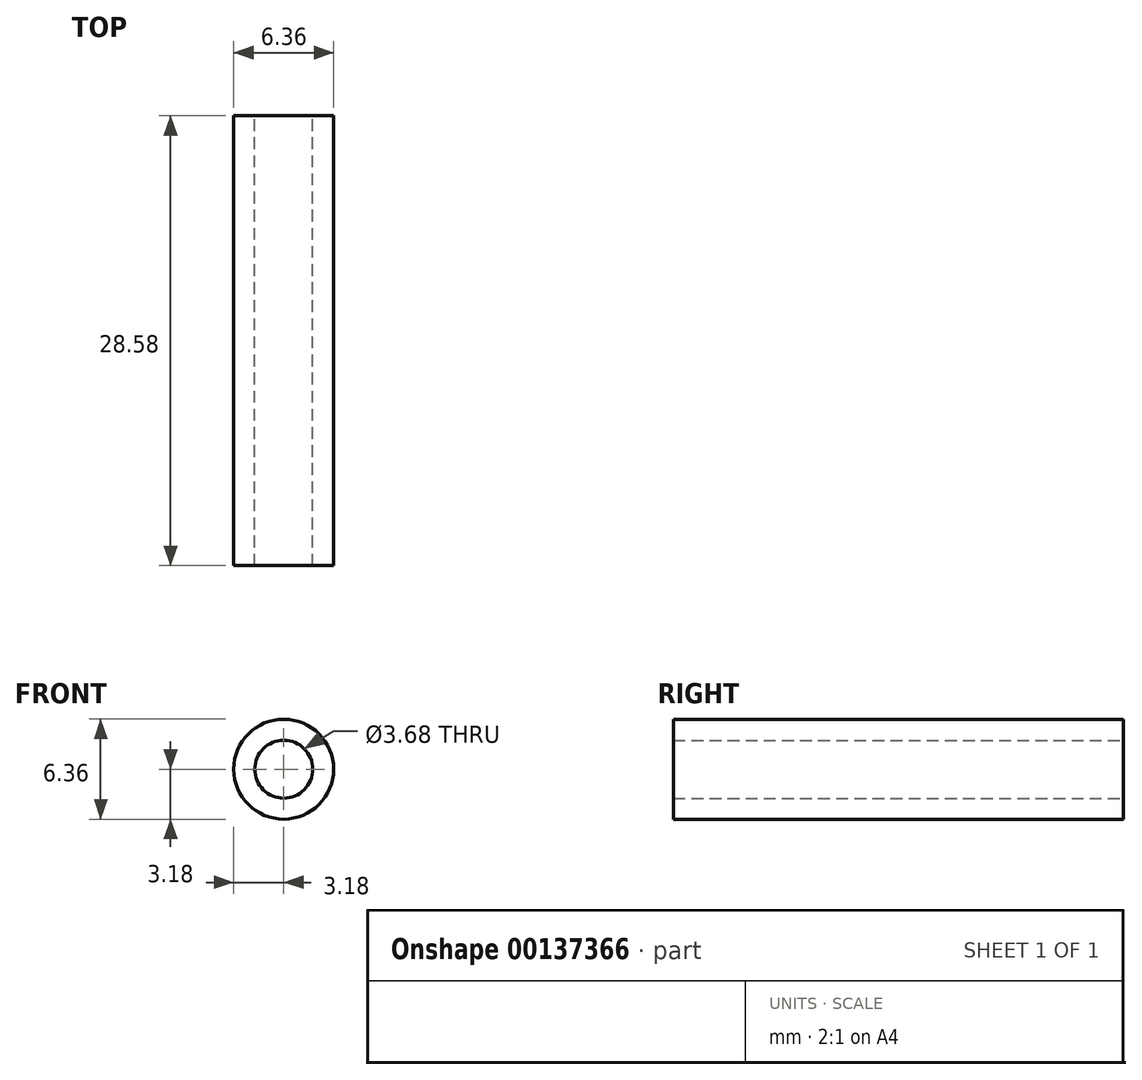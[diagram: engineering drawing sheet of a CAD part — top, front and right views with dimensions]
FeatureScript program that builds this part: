
annotation { "Feature Type Name" : "Feature", "Feature Type Description" : "" }
export const myFeature = defineFeature(function(context is Context, id is Id, definition is map)
    precondition{}
    {
        {
            var Q0;
            Q0=qCreatedBy(makeId("Front.planeOp"),FACE);
            var sketch = newSketch(context, id + "F0", { "sketchPlane" : qUnion([Q0])});
            skCircle(sketch, "E0", {"center": v(0, 0) * mm, "radius": 3.18 * mm});
            skCircle(sketch, "E1", {"center": v(0, 0) * mm, "radius": 1.84 * mm});
            skSolve(sketch);
        }
        {
            var Q0;
            Q0=makeQuery(id+"F0.imprint","IMPRINT",FACE,{"disambiguationData":[TD([[makeQuery(id+"F0.imprint","IMPRINT",EDGE,{"derivedFrom":sQuery(id+"F0.wireOp",EDGE,"E0")}),1.0]])]});
            extrude(context, id + "F1", {"entities" : qUnion([Q0]), "depth" : 28.57 * mm});
        }
    });
